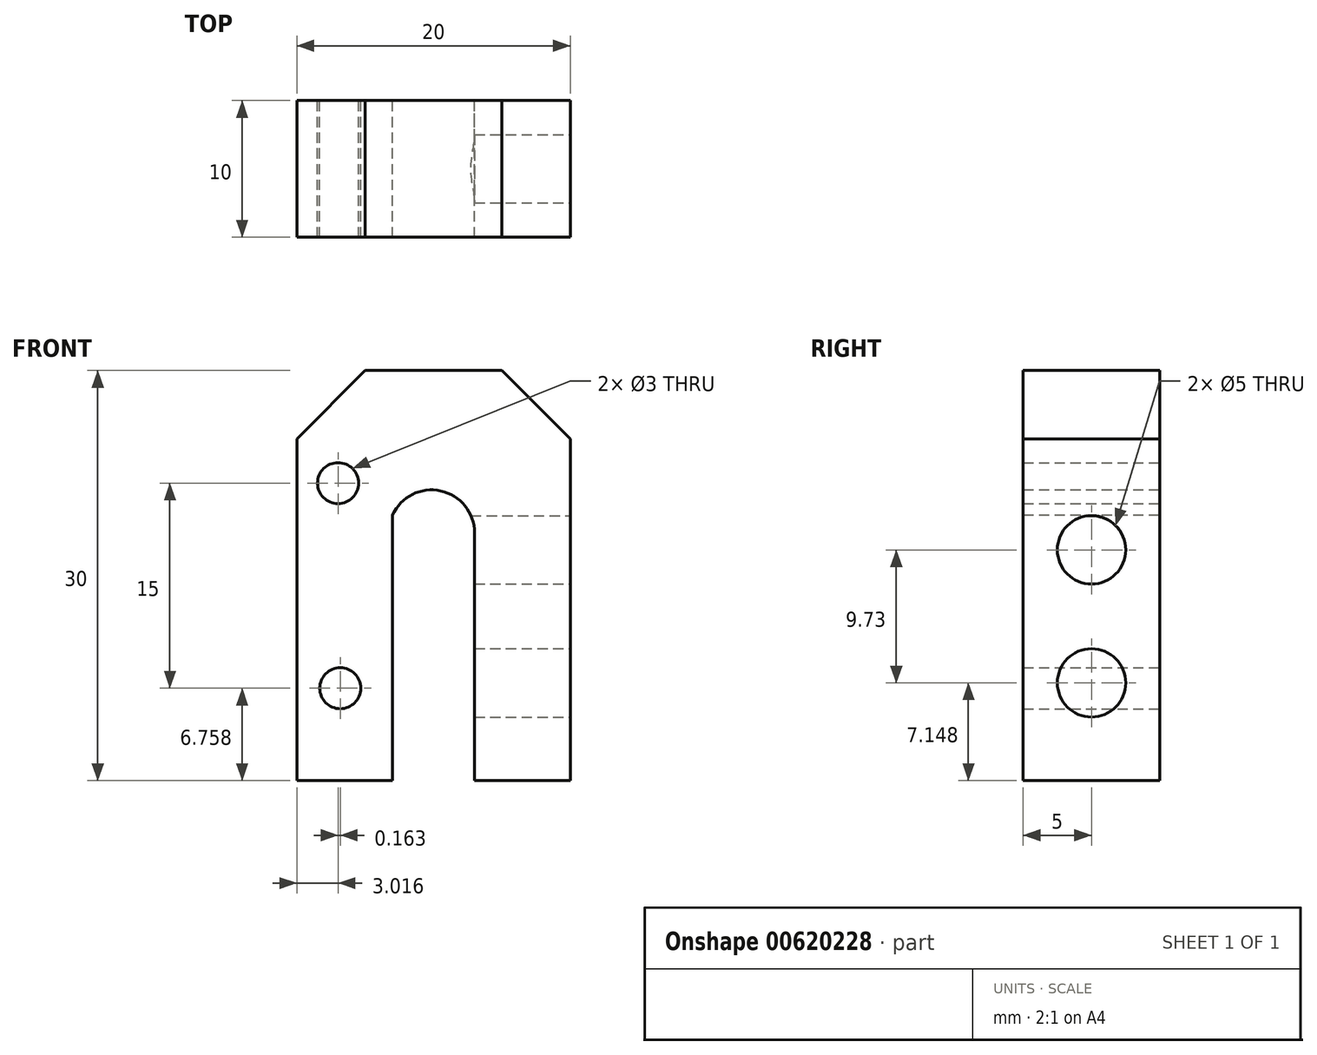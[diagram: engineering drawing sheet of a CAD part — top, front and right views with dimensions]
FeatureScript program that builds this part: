
annotation { "Feature Type Name" : "Feature", "Feature Type Description" : "" }
export const myFeature = defineFeature(function(context is Context, id is Id, definition is map)
    precondition{}
    {
        {
            var Q0;
            Q0=qCreatedBy(makeId("Front.planeOp"),FACE);
            var sketch = newSketch(context, id + "F0", { "sketchPlane" : qUnion([Q0])});
            skLineSegment(sketch, "E0.bottom", {"start": v(0, 0) * mm, "end": v(-7, 0) * mm});
            skLineSegment(sketch, "E0.top", {"start": v(0, 30) * mm, "end": v(-20, 30) * mm});
            skLineSegment(sketch, "E0.left", {"start": v(0, 0) * mm, "end": v(0, 30) * mm});
            skLineSegment(sketch, "E0.right", {"start": v(-20, 0) * mm, "end": v(-20, 30) * mm});
            skLineSegment(sketch, "E1.0", {"start": v(-7, 0) * mm, "end": v(-7, 18.12) * mm});
            skLineSegment(sketch, "E2.0", {"start": v(-13, 0) * mm, "end": v(-13, 19.43) * mm});
            skArc(sketch, "E3", {"start": v(-7, 18.12) * mm, "mid": v(-9.47, 21.2) * mm, "end": v(-13, 19.43) * mm});
            skPoint(sketch, "E4.start.orphan", {"position": v(-10, 0) * mm});
            skLineSegment(sketch, "E5.trimOffspring", {"start": v(-13, 0) * mm, "end": v(-20, 0) * mm});
            skSolve(sketch);
        }
        {
            var Q0;
            Q0 = qSketchRegion(id + "F0", true);
            extrude(context, id + "F1", {"entities" : qUnion([Q0]), "depth" : 10 * mm, "offsetDistance" : 25 * mm});
        }
        {
            var Q0;
            Q0=makeQuery(id+"F1.opExtrude","SWEPT_EDGE",EDGE,{"disambiguationData":[OSD([sQuery(id+"F0.wireOp",EDGE,"E0.top"),sQuery(id+"F0.wireOp",EDGE,"E0.left")])]});
            var Q1;
            Q1=makeQuery(id+"F1.opExtrude","SWEPT_EDGE",EDGE,{"disambiguationData":[OSD([sQuery(id+"F0.wireOp",EDGE,"E0.top"),sQuery(id+"F0.wireOp",EDGE,"E0.right")])]});
            chamfer(context, id + "F2", {"entities" : qUnion([Q0, Q1]), "width" : 5 * mm, "tangentPropagation" : true});
        }
        {
            var Q0;
            Q0=makeQuery(id+"F1.opExtrude","SWEPT_FACE",FACE,{"disambiguationData":[OSD([sQuery(id+"F0.wireOp",EDGE,"E0.left")])]});
            var sketch = newSketch(context, id + "F3", { "sketchPlane" : qUnion([Q0])});
            skCircle(sketch, "E6", {"center": v(-5, 16.88) * mm, "radius": 2.5 * mm});
            skPoint(sketch, "E6.centerSnap0", {"position": v(-5, 25) * mm});
            skCircle(sketch, "E7", {"center": v(-5, 7.15) * mm, "radius": 2.5 * mm});
            skSolve(sketch);
        }
        {
            var Q0;
            Q0 = qSketchRegion(id + "F3", true);
            extrude(context, id + "F4", {"entities" : qUnion([Q0]), "operationType" : NewBodyOperationType.REMOVE, "oppositeDirection" : true, "depth" : 10 * mm, "offsetDistance" : 25 * mm});
        }
        {
            var Q0;
            Q0=qCreatedBy(makeId("Front.planeOp"),FACE);
            var sketch = newSketch(context, id + "F5", { "sketchPlane" : qUnion([Q0])});
            skCircle(sketch, "E8", {"center": v(-16.98, 21.76) * mm, "radius": 1.5 * mm});
            skCircle(sketch, "E9", {"center": v(-16.82, 6.76) * mm, "radius": 1.5 * mm});
            skSolve(sketch);
        }
        {
            var Q0;
            Q0 = qSketchRegion(id + "F5", true);
            extrude(context, id + "F6", {"entities" : qUnion([Q0]), "operationType" : NewBodyOperationType.REMOVE, "depth" : 12 * mm, "offsetDistance" : 25 * mm});
        }
    });
